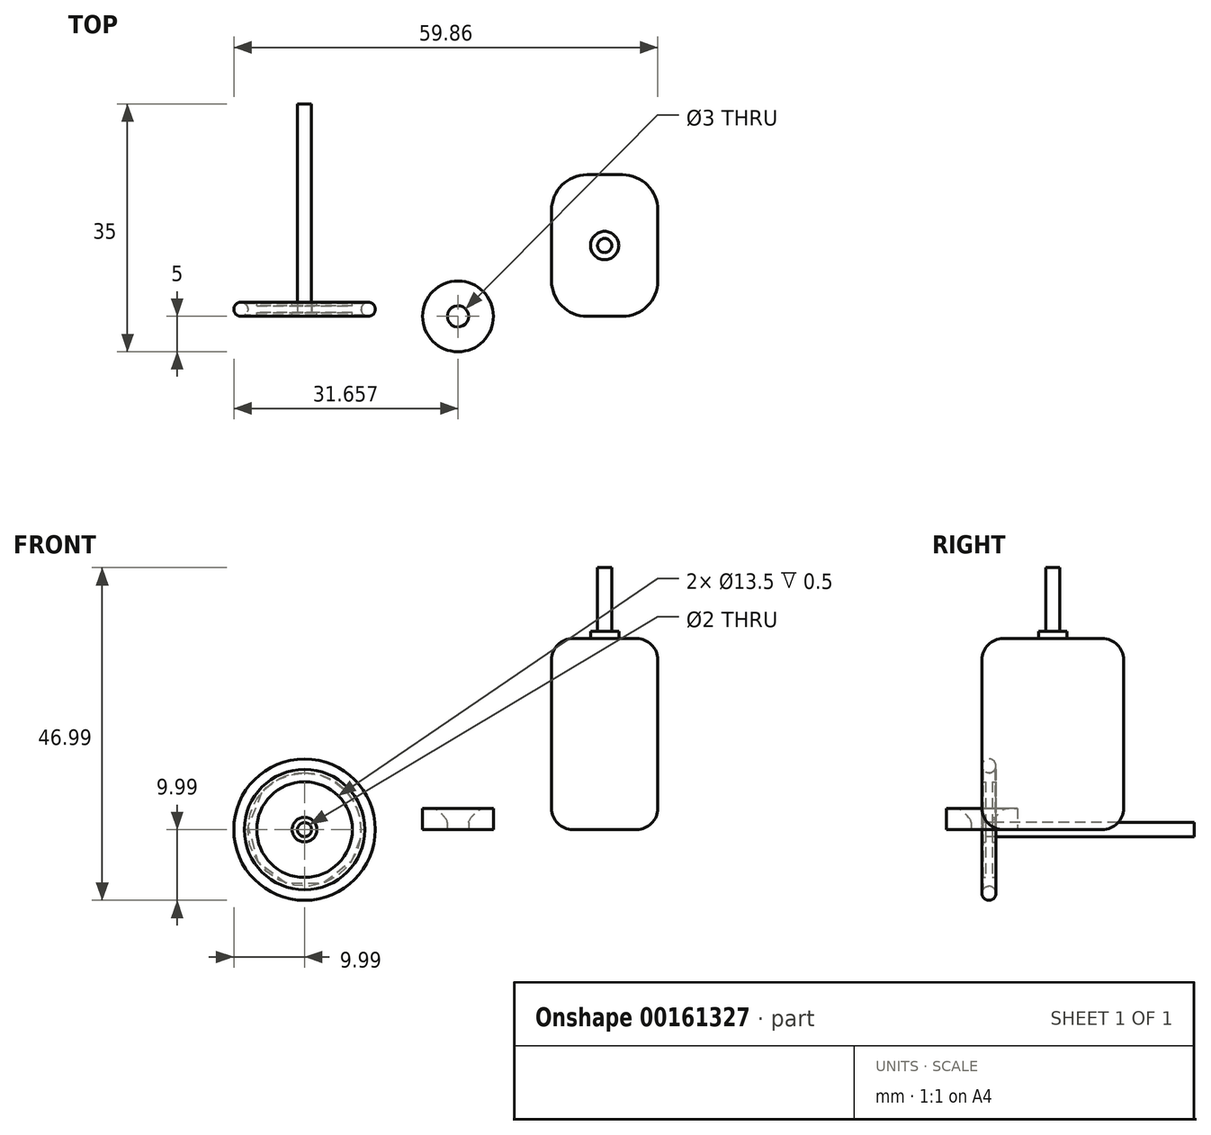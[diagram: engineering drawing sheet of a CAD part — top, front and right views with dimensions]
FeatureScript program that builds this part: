
annotation { "Feature Type Name" : "Feature", "Feature Type Description" : "" }
export const myFeature = defineFeature(function(context is Context, id is Id, definition is map)
    precondition{}
    {
        {
            var Q0;
            Q0=qCreatedBy(makeId("Right.planeOp"),FACE);
            var sketch = newSketch(context, id + "F0", { "sketchPlane" : qUnion([Q0])});
            skLineSegment(sketch, "E0", {"start": v(0, 0) * mm, "end": v(0, 1.75) * mm});
            skLineSegment(sketch, "E1", {"start": v(0, 1.75) * mm, "end": v(0.5, 1.75) * mm});
            skLineSegment(sketch, "E2", {"start": v(0.5, 1.75) * mm, "end": v(0.5, 6.75) * mm});
            skLineSegment(sketch, "E3", {"start": v(0.5, 6.75) * mm, "end": v(0, 6.75) * mm});
            skLineSegment(sketch, "E4", {"start": v(0, 6.75) * mm, "end": v(0, 8.5) * mm});
            skLineSegment(sketch, "E5", {"start": v(0, 8.5) * mm, "end": v(0.13, 8.5) * mm});
            skLineSegment(sketch, "E6", {"start": v(2, 8.5) * mm, "end": v(2, 6.75) * mm});
            skLineSegment(sketch, "E7", {"start": v(2, 6.75) * mm, "end": v(1.5, 6.75) * mm});
            skLineSegment(sketch, "E8", {"start": v(1.5, 6.75) * mm, "end": v(1.5, 1.75) * mm});
            skLineSegment(sketch, "E9", {"start": v(1.5, 1.75) * mm, "end": v(2, 1.75) * mm});
            skLineSegment(sketch, "E10", {"start": v(2, 1.75) * mm, "end": v(2, 0) * mm});
            skLineSegment(sketch, "E11", {"start": v(2, 0) * mm, "end": v(0, 0) * mm});
            skLineSegment(sketch, "E12", {"start": v(1, 0) * mm, "end": v(1, 8.5) * mm, "construction": true});
            skArc(sketch, "E13", {"start": v(0.13, 8.5) * mm, "mid": v(1, 8) * mm, "end": v(1.87, 8.5) * mm});
            skLineSegment(sketch, "E14.trimOffspring", {"start": v(1.87, 8.5) * mm, "end": v(2, 8.5) * mm});
            skCircle(sketch, "E15.0", {"center": v(1, 9) * mm, "radius": 0.99 * mm});
            skSolve(sketch);
        }
        {
            var Q0;
            Q0=makeQuery(id+"F0.imprint","IMPRINT",FACE,{"disambiguationData":[TD([[makeQuery(id+"F0.imprint","IMPRINT",EDGE,{"derivedFrom":sQuery(id+"F0.wireOp",EDGE,"E15.0")}),1.0]])]});
            var Q1;
            Q1=makeQuery(id+"F0.imprint","IMPRINT",FACE,{"disambiguationData":[TD([[makeQuery(id+"F0.imprint","IMPRINT",EDGE,{"derivedFrom":sQuery(id+"F0.wireOp",EDGE,"E0")}),-1.0]])]});
            var Q2;
            Q2=sQuery(id+"F0.wireOp",EDGE,"E11");
            revolve(context, id + "F1", {"entities" : qUnion([Q0, Q1]), "axis" : qUnion([Q2]), "revolveType" : RevolveType.FULL});
        }
        {
            var Q0;
            Q0=makeQuery(id+"F1.opRevolve","SWEPT_FACE",FACE,{"disambiguationData":[OSD([sQuery(id+"F0.wireOp",EDGE,"E0")])]});
            var sketch = newSketch(context, id + "F2", { "sketchPlane" : qUnion([Q0])});
            skCircle(sketch, "E16", {"center": v(0, 0) * mm, "radius": 1 * mm});
            skSolve(sketch);
        }
        {
            var Q0;
            Q0=makeQuery(id+"F2.imprint","IMPRINT",FACE,{"disambiguationData":[TD([[makeQuery(id+"F2.imprint","IMPRINT",EDGE,{"derivedFrom":sQuery(id+"F2.wireOp",EDGE,"E16")}),1.0]])]});
            extrude(context, id + "F3", {"entities" : qUnion([Q0]), "operationType" : NewBodyOperationType.REMOVE, "endBound" : BoundingType.THROUGH_ALL, "oppositeDirection" : true, "depth" : 25 * mm});
        }
        {
            var Q0;
            Q0=makeQuery(id+"F3.boolean.opBoolean","SPLIT",FACE,{"disambiguationData":[TD([makeQuery(id+"F3.opExtrude","SWEPT_FACE",FACE,{"disambiguationData":[OSD([sQuery(id+"F2.wireOp",EDGE,"E16")])]})])],"derivedFrom":makeQuery(id+"F1.opRevolve","SWEPT_FACE",FACE,{"disambiguationData":[OSD([sQuery(id+"F0.wireOp",EDGE,"E10")])]})});
            extrude(context, id + "F4", {"entities" : qUnion([Q0]), "operationType" : NewBodyOperationType.ADD, "depth" : 28 * mm});
        }
        {
            var Q0;
            Q0=qCreatedBy(makeId("Top.planeOp"),FACE);
            var sketch = newSketch(context, id + "F5", { "sketchPlane" : qUnion([Q0])});
            skCircle(sketch, "E17", {"center": v(21.67, 0) * mm, "radius": 5 * mm});
            skCircle(sketch, "E18", {"center": v(21.67, 0) * mm, "radius": 1.5 * mm});
            skLineSegment(sketch, "E19.bottom", {"start": v(34.87, 0) * mm, "end": v(49.87, 0) * mm});
            skLineSegment(sketch, "E19.top", {"start": v(34.87, 20) * mm, "end": v(49.87, 20) * mm});
            skLineSegment(sketch, "E19.left", {"start": v(34.87, 0) * mm, "end": v(34.87, 20) * mm});
            skLineSegment(sketch, "E19.right", {"start": v(49.87, 0) * mm, "end": v(49.87, 20) * mm});
            skCircle(sketch, "E20", {"center": v(60.22, 0) * mm, "radius": 5 * mm});
            skCircle(sketch, "E21", {"center": v(60.22, 0) * mm, "radius": 1 * mm});
            skLineSegment(sketch, "E22", {"start": v(57.15, 3.95) * mm, "end": v(57.23, 4.88) * mm});
            skLineSegment(sketch, "E23", {"start": v(57.23, 4.88) * mm, "end": v(58.14, 4.55) * mm});
            skCircle(sketch, "E24", {"center": v(42.1, 44.52) * mm, "radius": 3.27 * mm});
            skCircle(sketch, "E25", {"center": v(42.1, 44.52) * mm, "radius": 3.64 * mm, "construction": true});
            skCircle(sketch, "E26", {"center": v(42.1, 44.52) * mm, "radius": 4 * mm, "construction": true});
            skLineSegment(sketch, "E27", {"start": v(42.1, 44.52) * mm, "end": v(42.1, 55.3) * mm, "construction": true});
            skLineSegment(sketch, "E28", {"start": v(42.1, 44.52) * mm, "end": v(40.7, 62.52) * mm, "construction": true});
            skLineSegment(sketch, "E29", {"start": v(42.1, 48.16) * mm, "end": v(31.57, 48.16) * mm, "construction": true});
            skLineSegment(sketch, "E30", {"start": v(42.1, 48.16) * mm, "end": v(31.82, 44.41) * mm, "construction": true});
            skCircle(sketch, "E31", {"center": v(42.1, 48.16) * mm, "radius": 0.9 * mm, "construction": true});
            skCircle(sketch, "E32", {"center": v(41.25, 47.85) * mm, "radius": 0.9 * mm, "construction": true});
            skArc(sketch, "E33", {"start": v(40.4, 48.16) * mm, "mid": v(40.4, 48.15) * mm, "end": v(40.4, 48.13) * mm});
            skArc(sketch, "E34.trimOffspring", {"start": v(42.16, 47.8) * mm, "mid": v(42.04, 48.16) * mm, "end": v(41.87, 48.51) * mm});
            skArc(sketch, "E35.MirrorCS", {"start": v(41.54, 47.75) * mm, "mid": v(41.6, 48.13) * mm, "end": v(41.72, 48.5) * mm});
            skLineSegment(sketch, "E36", {"start": v(41.72, 48.5) * mm, "end": v(41.87, 48.51) * mm});
            skArc(sketch, "E37.1.0", {"start": v(41.15, 47.65) * mm, "mid": v(40.92, 47.97) * mm, "end": v(40.65, 48.25) * mm});
            skLineSegment(sketch, "E37.1.1", {"start": v(40.5, 48.19) * mm, "end": v(40.65, 48.25) * mm});
            skArc(sketch, "E37.1.2", {"start": v(40.58, 47.41) * mm, "mid": v(40.51, 47.8) * mm, "end": v(40.5, 48.19) * mm});
            skArc(sketch, "E37.2.0", {"start": v(40.23, 47.2) * mm, "mid": v(39.91, 47.43) * mm, "end": v(39.57, 47.61) * mm});
            skLineSegment(sketch, "E37.2.1", {"start": v(39.45, 47.51) * mm, "end": v(39.57, 47.61) * mm});
            skArc(sketch, "E37.2.2", {"start": v(39.76, 46.8) * mm, "mid": v(39.58, 47.14) * mm, "end": v(39.45, 47.51) * mm});
            skArc(sketch, "E37.3.0", {"start": v(39.5, 46.49) * mm, "mid": v(39.12, 46.61) * mm, "end": v(38.74, 46.68) * mm});
            skLineSegment(sketch, "E37.3.1", {"start": v(38.66, 46.55) * mm, "end": v(38.74, 46.68) * mm});
            skArc(sketch, "E37.3.2", {"start": v(39.17, 45.96) * mm, "mid": v(38.9, 46.23) * mm, "end": v(38.66, 46.55) * mm});
            skArc(sketch, "E37.4.0", {"start": v(39.01, 45.58) * mm, "mid": v(38.62, 45.59) * mm, "end": v(38.24, 45.53) * mm});
            skLineSegment(sketch, "E37.4.1", {"start": v(38.2, 45.38) * mm, "end": v(38.24, 45.53) * mm});
            skArc(sketch, "E37.4.2", {"start": v(38.87, 44.98) * mm, "mid": v(38.52, 45.16) * mm, "end": v(38.2, 45.38) * mm});
            skArc(sketch, "E37.5.0", {"start": v(38.84, 44.57) * mm, "mid": v(38.46, 44.46) * mm, "end": v(38.12, 44.28) * mm});
            skLineSegment(sketch, "E37.5.1", {"start": v(38.13, 44.13) * mm, "end": v(38.12, 44.28) * mm});
            skArc(sketch, "E37.5.2", {"start": v(38.88, 43.96) * mm, "mid": v(38.5, 44.02) * mm, "end": v(38.13, 44.13) * mm});
            skArc(sketch, "E37.6.0", {"start": v(38.98, 43.56) * mm, "mid": v(38.66, 43.33) * mm, "end": v(38.38, 43.06) * mm});
            skLineSegment(sketch, "E37.6.1", {"start": v(38.44, 42.92) * mm, "end": v(38.38, 43.06) * mm});
            skArc(sketch, "E37.6.2", {"start": v(39.22, 42.99) * mm, "mid": v(38.83, 42.93) * mm, "end": v(38.44, 42.92) * mm});
            skArc(sketch, "E37.7.0", {"start": v(39.43, 42.64) * mm, "mid": v(39.2, 42.33) * mm, "end": v(39.02, 41.98) * mm});
            skLineSegment(sketch, "E37.7.1", {"start": v(39.12, 41.87) * mm, "end": v(39.02, 41.98) * mm});
            skArc(sketch, "E37.7.2", {"start": v(39.83, 42.17) * mm, "mid": v(39.49, 42) * mm, "end": v(39.12, 41.87) * mm});
            skArc(sketch, "E37.8.0", {"start": v(40.14, 41.9) * mm, "mid": v(40.02, 41.54) * mm, "end": v(39.95, 41.15) * mm});
            skLineSegment(sketch, "E37.8.1", {"start": v(40.08, 41.07) * mm, "end": v(39.95, 41.15) * mm});
            skArc(sketch, "E37.8.2", {"start": v(40.67, 41.58) * mm, "mid": v(40.4, 41.3) * mm, "end": v(40.08, 41.07) * mm});
            skArc(sketch, "E37.9.0", {"start": v(41.05, 41.43) * mm, "mid": v(41.04, 41.04) * mm, "end": v(41.1, 40.65) * mm});
            skLineSegment(sketch, "E37.9.1", {"start": v(41.25, 40.61) * mm, "end": v(41.1, 40.65) * mm});
            skArc(sketch, "E37.9.2", {"start": v(41.65, 41.28) * mm, "mid": v(41.47, 40.93) * mm, "end": v(41.25, 40.61) * mm});
            skArc(sketch, "E37.10.0", {"start": v(42.05, 41.25) * mm, "mid": v(42.17, 40.88) * mm, "end": v(42.35, 40.53) * mm});
            skLineSegment(sketch, "E37.10.1", {"start": v(42.5, 40.54) * mm, "end": v(42.35, 40.53) * mm});
            skArc(sketch, "E37.10.2", {"start": v(42.67, 41.3) * mm, "mid": v(42.61, 40.91) * mm, "end": v(42.5, 40.54) * mm});
            skArc(sketch, "E37.11.0", {"start": v(43.07, 41.4) * mm, "mid": v(43.3, 41.08) * mm, "end": v(43.57, 40.8) * mm});
            skLineSegment(sketch, "E37.11.1", {"start": v(43.7, 40.86) * mm, "end": v(43.57, 40.8) * mm});
            skArc(sketch, "E37.11.2", {"start": v(43.64, 41.63) * mm, "mid": v(43.7, 41.25) * mm, "end": v(43.7, 40.86) * mm});
            skArc(sketch, "E37.12.0", {"start": v(43.99, 41.84) * mm, "mid": v(44.3, 41.61) * mm, "end": v(44.65, 41.43) * mm});
            skLineSegment(sketch, "E37.12.1", {"start": v(44.76, 41.53) * mm, "end": v(44.65, 41.43) * mm});
            skArc(sketch, "E37.12.2", {"start": v(44.46, 42.25) * mm, "mid": v(44.64, 41.9) * mm, "end": v(44.76, 41.53) * mm});
            skArc(sketch, "E37.13.0", {"start": v(44.72, 42.55) * mm, "mid": v(45.1, 42.43) * mm, "end": v(45.48, 42.37) * mm});
            skLineSegment(sketch, "E37.13.1", {"start": v(45.56, 42.5) * mm, "end": v(45.48, 42.37) * mm});
            skArc(sketch, "E37.13.2", {"start": v(45.05, 43.08) * mm, "mid": v(45.33, 42.8) * mm, "end": v(45.56, 42.5) * mm});
            skArc(sketch, "E37.14.0", {"start": v(45.2, 43.46) * mm, "mid": v(45.6, 43.46) * mm, "end": v(45.98, 43.51) * mm});
            skLineSegment(sketch, "E37.14.1", {"start": v(46.01, 43.66) * mm, "end": v(45.98, 43.51) * mm});
            skArc(sketch, "E37.14.2", {"start": v(45.35, 44.06) * mm, "mid": v(45.7, 43.89) * mm, "end": v(46.01, 43.66) * mm});
            skArc(sketch, "E37.15.0", {"start": v(45.38, 44.47) * mm, "mid": v(45.75, 44.59) * mm, "end": v(46.1, 44.76) * mm});
            skLineSegment(sketch, "E37.15.1", {"start": v(46.09, 44.91) * mm, "end": v(46.1, 44.76) * mm});
            skArc(sketch, "E37.15.2", {"start": v(45.33, 45.09) * mm, "mid": v(45.72, 45.03) * mm, "end": v(46.09, 44.91) * mm});
            skArc(sketch, "E37.16.0", {"start": v(45.24, 45.48) * mm, "mid": v(45.55, 45.7) * mm, "end": v(45.83, 45.98) * mm});
            skLineSegment(sketch, "E37.16.1", {"start": v(45.77, 46.12) * mm, "end": v(45.83, 45.98) * mm});
            skArc(sketch, "E37.16.2", {"start": v(45, 46.05) * mm, "mid": v(45.38, 46.12) * mm, "end": v(45.77, 46.12) * mm});
            skArc(sketch, "E37.17.0", {"start": v(44.79, 46.4) * mm, "mid": v(45.02, 46.72) * mm, "end": v(45.2, 47.06) * mm});
            skLineSegment(sketch, "E37.17.1", {"start": v(45.1, 47.18) * mm, "end": v(45.2, 47.06) * mm});
            skArc(sketch, "E37.17.2", {"start": v(44.38, 46.87) * mm, "mid": v(44.73, 47.05) * mm, "end": v(45.1, 47.18) * mm});
            skArc(sketch, "E37.18.0", {"start": v(44.07, 47.14) * mm, "mid": v(44.2, 47.5) * mm, "end": v(44.26, 47.9) * mm});
            skLineSegment(sketch, "E37.18.1", {"start": v(44.13, 47.97) * mm, "end": v(44.26, 47.9) * mm});
            skArc(sketch, "E37.18.2", {"start": v(43.55, 47.46) * mm, "mid": v(43.82, 47.74) * mm, "end": v(44.13, 47.97) * mm});
            skArc(sketch, "E37.19.0", {"start": v(43.17, 47.62) * mm, "mid": v(43.17, 48) * mm, "end": v(43.12, 48.4) * mm});
            skLineSegment(sketch, "E37.19.1", {"start": v(42.97, 48.43) * mm, "end": v(43.12, 48.4) * mm});
            skArc(sketch, "E37.19.2", {"start": v(42.57, 47.76) * mm, "mid": v(42.74, 48.1) * mm, "end": v(42.97, 48.43) * mm});
            skCircle(sketch, "E38", {"center": v(42.1, 44.52) * mm, "radius": 1 * mm});
            skSolve(sketch);
        }
        {
            var Q0;
            Q0=makeQuery(id+"F5.imprint","IMPRINT",FACE,{"disambiguationData":[TD([[makeQuery(id+"F5.imprint","IMPRINT",EDGE,{"derivedFrom":sQuery(id+"F5.wireOp",EDGE,"E17")}),1.0]])]});
            extrude(context, id + "F6", {"entities" : qUnion([Q0]), "depth" : 3 * mm});
        }
        {
            var Q0;
            Q0=makeQuery(id+"F6.opExtrude","CAP_EDGE",EDGE,{"disambiguationData":[OSD([sQuery(id+"F5.wireOp",EDGE,"E18")])],"isStart":false});
            fillet(context, id + "F7", {"entities" : qUnion([Q0]), "radius" : 2 * mm, "tangentPropagation" : true, "rho" : 0.2, "crossSection" : FilletCrossSection.CONIC, "allowEdgeOverflow" : false});
        }
        {
            var Q0;
            Q0=makeQuery(id+"F5.imprint","IMPRINT",FACE,{"disambiguationData":[TD([[makeQuery(id+"F5.imprint","IMPRINT",EDGE,{"derivedFrom":sQuery(id+"F5.wireOp",EDGE,"E19.bottom")}),1.0]])]});
            extrude(context, id + "F8", {"entities" : qUnion([Q0]), "depth" : 27 * mm});
        }
        {
            var Q0;
            Q0=makeQuery(id+"F8.opExtrude","SWEPT_EDGE",EDGE,{"disambiguationData":[OSD([sQuery(id+"F5.wireOp",EDGE,"E19.top"),sQuery(id+"F5.wireOp",EDGE,"E19.left")])]});
            var Q1;
            Q1=makeQuery(id+"F8.opExtrude","SWEPT_EDGE",EDGE,{"disambiguationData":[OSD([sQuery(id+"F5.wireOp",EDGE,"E19.top"),sQuery(id+"F5.wireOp",EDGE,"E19.right")])]});
            var Q2;
            Q2=makeQuery(id+"F8.opExtrude","SWEPT_EDGE",EDGE,{"disambiguationData":[OSD([sQuery(id+"F5.wireOp",EDGE,"E19.bottom"),sQuery(id+"F5.wireOp",EDGE,"E19.left")])]});
            var Q3;
            Q3=makeQuery(id+"F8.opExtrude","SWEPT_EDGE",EDGE,{"disambiguationData":[OSD([sQuery(id+"F5.wireOp",EDGE,"E19.bottom"),sQuery(id+"F5.wireOp",EDGE,"E19.right")])]});
            fillet(context, id + "F9", {"entities" : qUnion([Q0, Q1, Q2, Q3]), "radius" : 5 * mm, "tangentPropagation" : true, "allowEdgeOverflow" : false});
        }
        {
            var Q0;
            Q0=makeQuery(id+"F8.opExtrude","CAP_EDGE",EDGE,{"disambiguationData":[OSD([sQuery(id+"F5.wireOp",EDGE,"E19.top")])],"isStart":false});
            var Q1;
            Q1=makeQuery(id+"F8.opExtrude","CAP_FACE",FACE,{"disambiguationData":[OSD([sQuery(id+"F5.wireOp",EDGE,"E19.bottom"),sQuery(id+"F5.wireOp",EDGE,"E19.top"),sQuery(id+"F5.wireOp",EDGE,"E19.left"),sQuery(id+"F5.wireOp",EDGE,"E19.right")])],"isStart":true});
            fillet(context, id + "F10", {"entities" : qUnion([Q0, Q1]), "radius" : 3 * mm, "tangentPropagation" : true, "allowEdgeOverflow" : false});
        }
        {
            var Q0;
            Q0=makeQuery(id+"F8.opExtrude","CAP_FACE",FACE,{"disambiguationData":[OSD([sQuery(id+"F5.wireOp",EDGE,"E19.bottom"),sQuery(id+"F5.wireOp",EDGE,"E19.top"),sQuery(id+"F5.wireOp",EDGE,"E19.left"),sQuery(id+"F5.wireOp",EDGE,"E19.right")])],"isStart":false});
            var sketch = newSketch(context, id + "F11", { "sketchPlane" : qUnion([Q0])});
            skCircle(sketch, "E39", {"center": v(42.37, 10) * mm, "radius": 1 * mm});
            skPoint(sketch, "E39.centerSnap0", {"position": v(37.87, 10) * mm});
            skPoint(sketch, "E39.centerSnap1", {"position": v(42.37, 17) * mm});
            skCircle(sketch, "E40", {"center": v(42.37, 10) * mm, "radius": 2 * mm});
            skSolve(sketch);
        }
        {
            var Q0;
            Q0=makeQuery(id+"F11.imprint","IMPRINT",FACE,{"disambiguationData":[TD([[makeQuery(id+"F11.imprint","IMPRINT",EDGE,{"derivedFrom":sQuery(id+"F11.wireOp",EDGE,"E39")}),1.0]])]});
            extrude(context, id + "F12", {"entities" : qUnion([Q0]), "depth" : 10 * mm});
        }
        {
            var Q0;
            Q0=makeQuery(id+"F11.imprint","IMPRINT",FACE,{"disambiguationData":[TD([[makeQuery(id+"F11.imprint","IMPRINT",EDGE,{"derivedFrom":sQuery(id+"F11.wireOp",EDGE,"E39")}),-1.0]])]});
            extrude(context, id + "F13", {"entities" : qUnion([Q0]), "operationType" : NewBodyOperationType.ADD, "depth" : 1 * mm});
        }
    });
